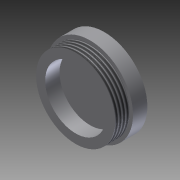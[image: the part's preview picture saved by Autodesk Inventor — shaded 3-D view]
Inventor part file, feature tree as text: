
AUTODESK INVENTOR PART (.ipt)
format: ipt  version: 2011 (Build 150239000, 239)  size: 96,768 bytes
history: native  units: in
note: dims shown in document units (in); Inventor stores cm internally (conversion verified against a paired STEP export)
features: extrude x3, sketch x3, thread x1
ambient origin geometry x8: Origin, YZ Plane, XZ Plane, XY Plane, X Axis, Y Axis, Z Axis, Center Point
bodies: Solid1 (feature_tree)
feature tree (7):
  extrude  "Extrusion1"  Depth=0.1in TaperAngle=0.0deg
  extrude  "Extrusion2"  Depth=0.1in TaperAngle=0.0deg
  thread  "Thread1"  [1 undecoded]
  extrude  "Extrusion3"  Depth=0.1in TaperAngle=0.0deg
  sketch  "Sketch1"  dims[d0=0.6in d1=0.1in d2=0.0in]
  sketch  "Sketch2"  dims[d3=0.552in d4=0.1in d5=0.0in d6=1.0in d7=0.0in]
  sketch  "Sketch3"  dims[d8=0.425in d9=0.1in d10=0.0in]
note: 1 required parameter value undecoded (feature->parameter linkage not recoverable at this tier; creation-order binding heuristic only, values carry confidence <= 0.55)
